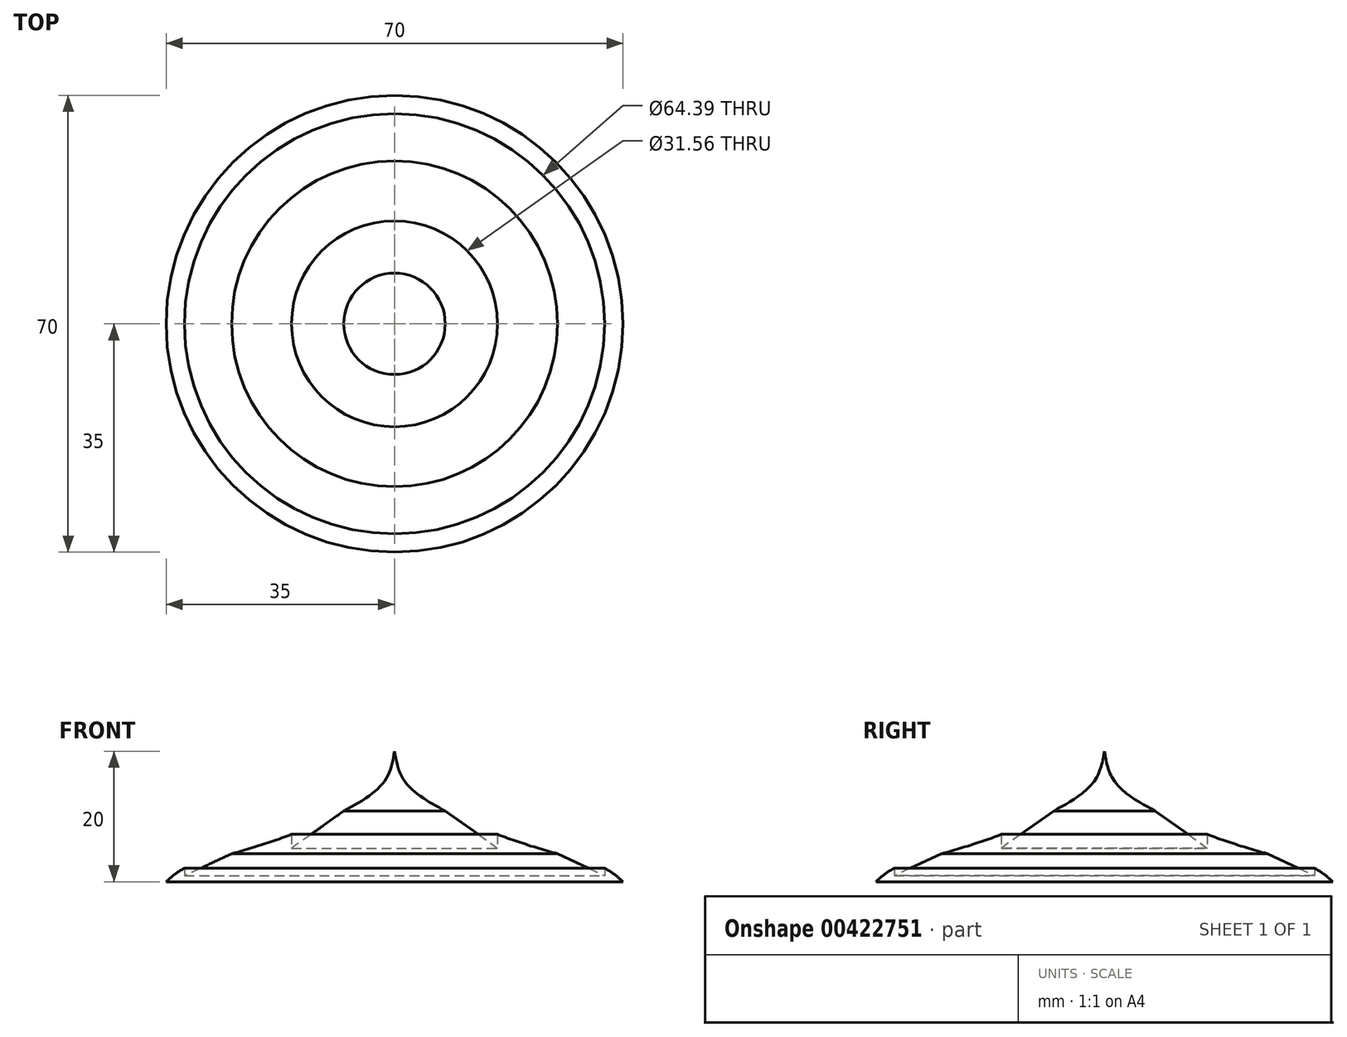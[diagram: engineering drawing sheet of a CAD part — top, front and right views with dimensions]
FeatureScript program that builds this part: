
annotation { "Feature Type Name" : "Feature", "Feature Type Description" : "" }
export const myFeature = defineFeature(function(context is Context, id is Id, definition is map)
    precondition{}
    {
        {
            var Q0;
            Q0=qCreatedBy(makeId("Front.planeOp"),FACE);
            var sketch = newSketch(context, id + "F0", { "sketchPlane" : qUnion([Q0])});
            skLineSegment(sketch, "E0", {"start": v(0, 0) * mm, "end": v(0, 20) * mm});
            skLineSegment(sketch, "E1", {"start": v(0, 0) * mm, "end": v(-35, 0) * mm});
            skFitSpline(sketch, "E2", {"points": [v(0, 20) * mm, v(-1.6, 15.32) * mm, v(-7.77, 10.86) * mm, v(-15.78, 7.25) * mm, v(-24.97, 4.3) * mm, v(-32.2, 2.06) * mm, v(-35, 0) * mm], "startDerivative": vector(-5.92, -34.43) * mm, "endDerivative": vector(-20.06, -18.4) * mm});
            skLineSegment(sketch, "E3", {"start": v(-15.78, 7.25) * mm, "end": v(-15.78, 5.15) * mm});
            skLineSegment(sketch, "E4", {"start": v(-15.78, 5.15) * mm, "end": v(-7.77, 10.86) * mm});
            skLineSegment(sketch, "E5", {"start": v(-32.2, 2.06) * mm, "end": v(-32.2, 0.91) * mm});
            skLineSegment(sketch, "E6", {"start": v(-32.2, 0.91) * mm, "end": v(-24.97, 4.3) * mm});
            skSolve(sketch);
        }
        {
            var Q0;
            {var subQ3=sQuery(id+"F0.wireOp",EDGE,"E0");Q0=makeQuery(id+"F0.imprint","IMPRINT",FACE,{"disambiguationData":[TD([[makeQuery(id+"F0.imprint","IMPRINT",EDGE,{"derivedFrom":subQ3}),1.0]])]});}
            var Q1;
            Q1=sQuery(id+"F0.wireOp",EDGE,"E0");
            revolve(context, id + "F1", {"entities" : qUnion([Q0]), "axis" : qUnion([Q1]), "revolveType" : RevolveType.FULL});
        }
    });
